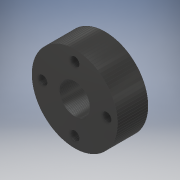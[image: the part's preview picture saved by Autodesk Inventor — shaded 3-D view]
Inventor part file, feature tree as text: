
AUTODESK INVENTOR PART (.ipt)
format: ipt  version: 2019 (Build 230136000, 136)  size: 1,536,000 bytes
history: native  units: in
note: dims shown in document units (in); Inventor stores cm internally (conversion verified against a paired STEP export)
features: other x6, direct_edit x2, plane x2, surface_op x1
ambient origin geometry x8: Origin, YZ Plane, XZ Plane, XY Plane, X Axis, Y Axis, Z Axis, Center Point
bodies: Solid1 (feature_tree)
feature tree (11):
  other  "shoulder_spacer"
  surface_op  "Stitch Surface1"
  direct_edit  "Direct Edit1"
  direct_edit  "Direct Edit2"
  plane  "Work Plane3"
  other  "Work Axis2"
  plane  "Work Plane4"
  other  "Composite1"
  other  "Srf1"
  other  "Scale1"
  other  "Scale2"
